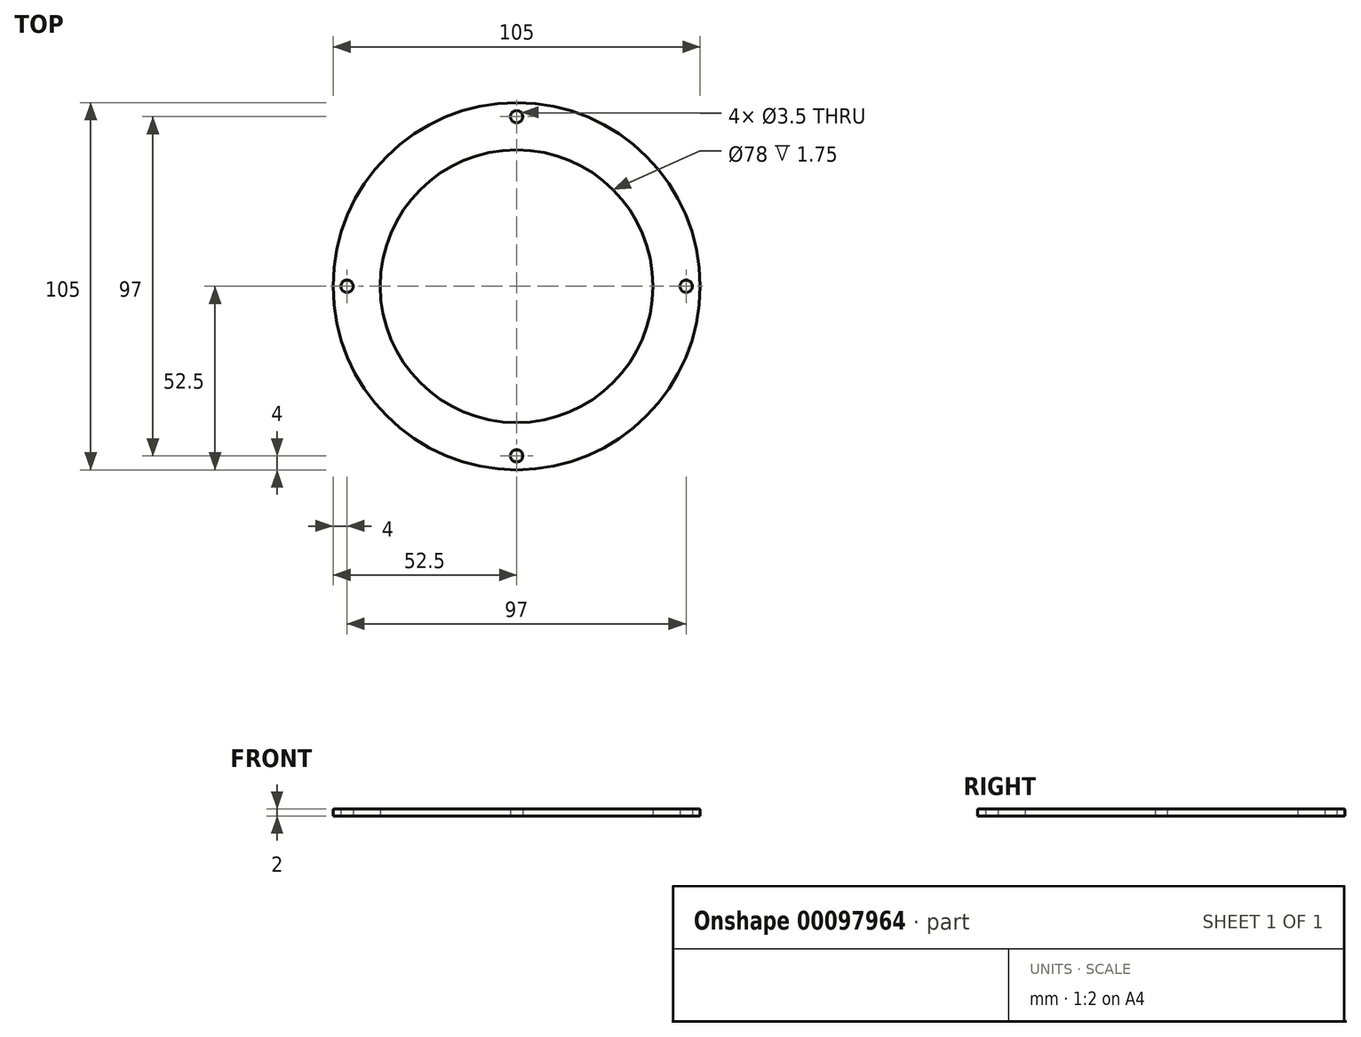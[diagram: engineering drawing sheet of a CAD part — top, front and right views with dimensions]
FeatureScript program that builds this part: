
annotation { "Feature Type Name" : "Feature", "Feature Type Description" : "" }
export const myFeature = defineFeature(function(context is Context, id is Id, definition is map)
    precondition{}
    {
        {
            var Q0;
            Q0=qCreatedBy(makeId("Top.planeOp"),FACE);
            var sketch = newSketch(context, id + "F0", { "sketchPlane" : qUnion([Q0])});
            skCircle(sketch, "E0", {"center": v(0, 0) * mm, "radius": 39 * mm});
            skCircle(sketch, "E1", {"center": v(0, 0) * mm, "radius": 52.5 * mm});
            skSolve(sketch);
        }
        {
            var Q0;
            Q0 = qSketchRegion(id + "F0", true);
            extrude(context, id + "F1", {"entities" : qUnion([Q0]), "depth" : 2 * mm});
        }
        {
            var Q0;
            Q0=makeQuery(id+"F1.opExtrude","CAP_FACE",FACE,{"disambiguationData":[OSD([sQuery(id+"F0.wireOp",EDGE,"E0"),sQuery(id+"F0.wireOp",EDGE,"E1")])],"isStart":false});
            fillet(context, id + "F2", {"entities" : qUnion([Q0]), "radius" : 0.25 * mm, "tangentPropagation" : true, "allowEdgeOverflow" : false});
        }
        {
            var Q0;
            Q0=qCreatedBy(makeId("Top.planeOp"),FACE);
            var sketch = newSketch(context, id + "F3", { "sketchPlane" : qUnion([Q0])});
            skCircle(sketch, "E2", {"center": v(0, 0) * mm, "radius": 48.5 * mm, "construction": true});
            skCircle(sketch, "E3", {"center": v(48.5, 0) * mm, "radius": 1.75 * mm});
            skCircle(sketch, "E4", {"center": v(0, 48.5) * mm, "radius": 1.75 * mm});
            skCircle(sketch, "E5", {"center": v(-48.5, 0) * mm, "radius": 1.75 * mm});
            skCircle(sketch, "E6", {"center": v(0, -48.5) * mm, "radius": 1.75 * mm});
            skSolve(sketch);
        }
        {
            var Q0;
            Q0 = qSketchRegion(id + "F3", true);
            extrude(context, id + "F4", {"entities" : qUnion([Q0]), "operationType" : NewBodyOperationType.REMOVE, "endBound" : BoundingType.THROUGH_ALL, "depth" : 25 * mm});
        }
    });
